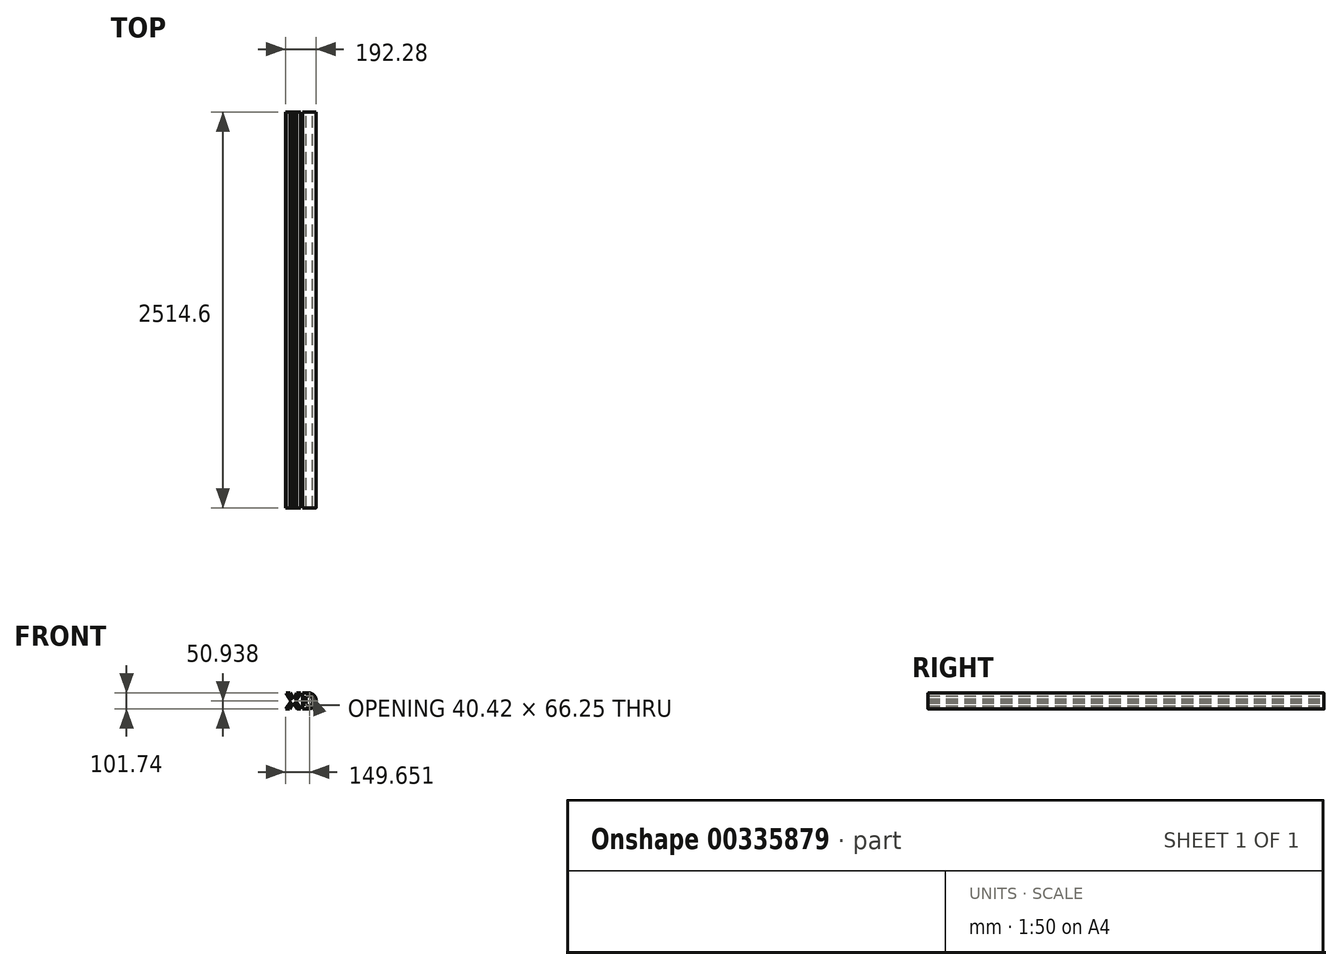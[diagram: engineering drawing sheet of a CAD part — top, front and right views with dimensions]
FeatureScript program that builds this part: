
annotation { "Feature Type Name" : "Feature", "Feature Type Description" : "" }
export const myFeature = defineFeature(function(context is Context, id is Id, definition is map)
    precondition{}
    {
        {
            var Q0;
            Q0=qCreatedBy(makeId("Front.planeOp"),FACE);
            var sketch = newSketch(context, id + "F0", { "sketchPlane" : qUnion([Q0])});
            skText(sketch, "E0", { "text": "XD", "fontName": "OpenSans-Bold.ttf"});
            const initialGuessF0  = {"E0": [-0.07135, -0.06526, 1, 0, 0.10261]};
            skSetInitialGuess(sketch, initialGuessF0);
            skSolve(sketch);
        }
        {
            var Q0;
            Q0=makeQuery(id+"F0.imprint","IMPRINT",FACE,{"disambiguationData":[TD([[makeQuery(id+"F0.imprint","IMPRINT",EDGE,{"derivedFrom":sQuery(id+"F0.wireOp",EDGE,"E0.sketch_text.stroke-0")}),-1.0]])]});
            extrude(context, id + "F1", {"entities" : qUnion([Q0]), "depth" : 2514.6 * mm});
        }
        {
            var Q0;
            Q0 = qSketchRegion(id + "F0", true);
            extrude(context, id + "F2", {"entities" : qUnion([Q0]), "operationType" : NewBodyOperationType.ADD, "depth" : 2514.6 * mm});
        }
    });
